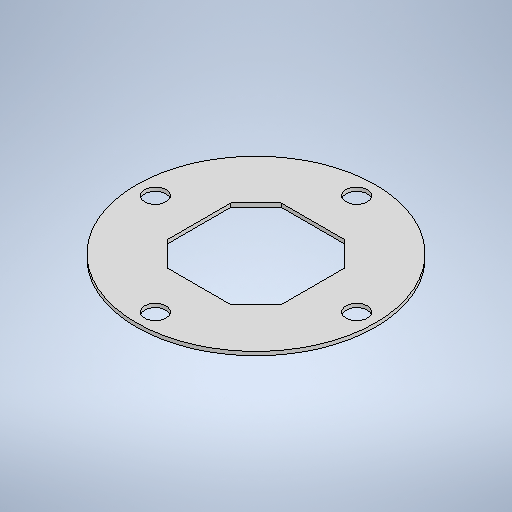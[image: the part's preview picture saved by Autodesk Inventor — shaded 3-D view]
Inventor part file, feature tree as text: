
AUTODESK INVENTOR PART (.ipt)
format: ipt  version: 2025.1 (Build 291241020, 241B)  size: 318,464 bytes
history: native  units: mm
features: other x4, sketch x2, sheet_metal_op x1, pattern_circular x1
ambient origin geometry x8: Origin, YZ Plane, XZ Plane, XY Plane, X Axis, Y Axis, Z Axis, Center Point
bodies: Body1 (feature_tree)
feature tree (8):
  sheet_metal_op  "Face3"
  pattern_circular  "Circular Pattern1"  Count=50  [1 undecoded]
  other  "Corner Chamfer2"
  sketch  "Sketch1"  dims[d156=3.0mm]
  other  "Plate5"
  sketch  "Sketch7"  dims[d157=190.0mm d158=90.0mm d159=90.0mm d160=17.0mm d161=80.0mm d162=3.0mm d163=0.0mm d164=40.0mm d165=360.0deg d167=20.0mm d168=6.0mm d169=45.0deg]
  other  "Cut1"
  other  "Definition1"
note: 1 required parameter value undecoded (feature->parameter linkage not recoverable at this tier; creation-order binding heuristic only, values carry confidence <= 0.55)
